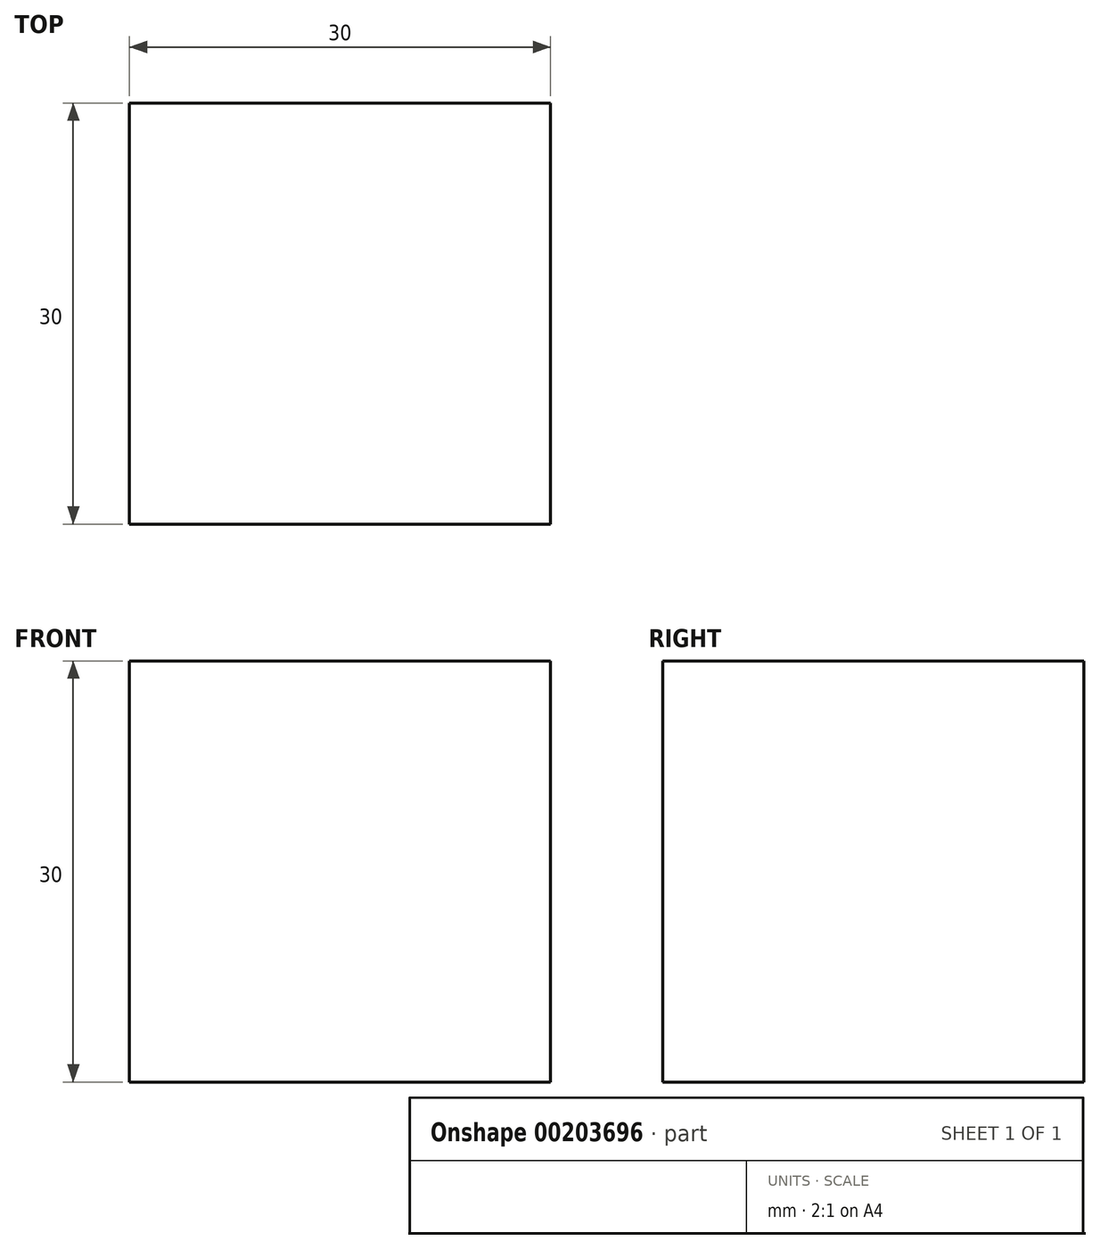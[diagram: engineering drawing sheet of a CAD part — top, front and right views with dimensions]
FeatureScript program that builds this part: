
annotation { "Feature Type Name" : "Feature", "Feature Type Description" : "" }
export const myFeature = defineFeature(function(context is Context, id is Id, definition is map)
    precondition{}
    {
        {
            var Q0;
            Q0=qCreatedBy(makeId("Top.planeOp"),FACE);
            var sketch = newSketch(context, id + "F0", { "sketchPlane" : qUnion([Q0])});
            skLineSegment(sketch, "E0.bottom", {"start": v(-15, 15) * mm, "end": v(15, 15) * mm});
            skLineSegment(sketch, "E0.top", {"start": v(-15, -15) * mm, "end": v(15, -15) * mm});
            skLineSegment(sketch, "E0.left", {"start": v(-15, 15) * mm, "end": v(-15, -15) * mm});
            skLineSegment(sketch, "E0.right", {"start": v(15, 15) * mm, "end": v(15, -15) * mm});
            skPoint(sketch, "E0.middle", {"position": v(0, 0) * mm});
            skSolve(sketch);
        }
        {
            var Q0;
            Q0=makeQuery(id+"F0.imprint","IMPRINT",FACE,{"disambiguationData":[TD([[makeQuery(id+"F0.imprint","IMPRINT",EDGE,{"derivedFrom":sQuery(id+"F0.wireOp",EDGE,"E0.bottom")}),-1.0]])]});
            extrude(context, id + "F1", {"entities" : qUnion([Q0]), "depth" : 30 * mm});
        }
    });
